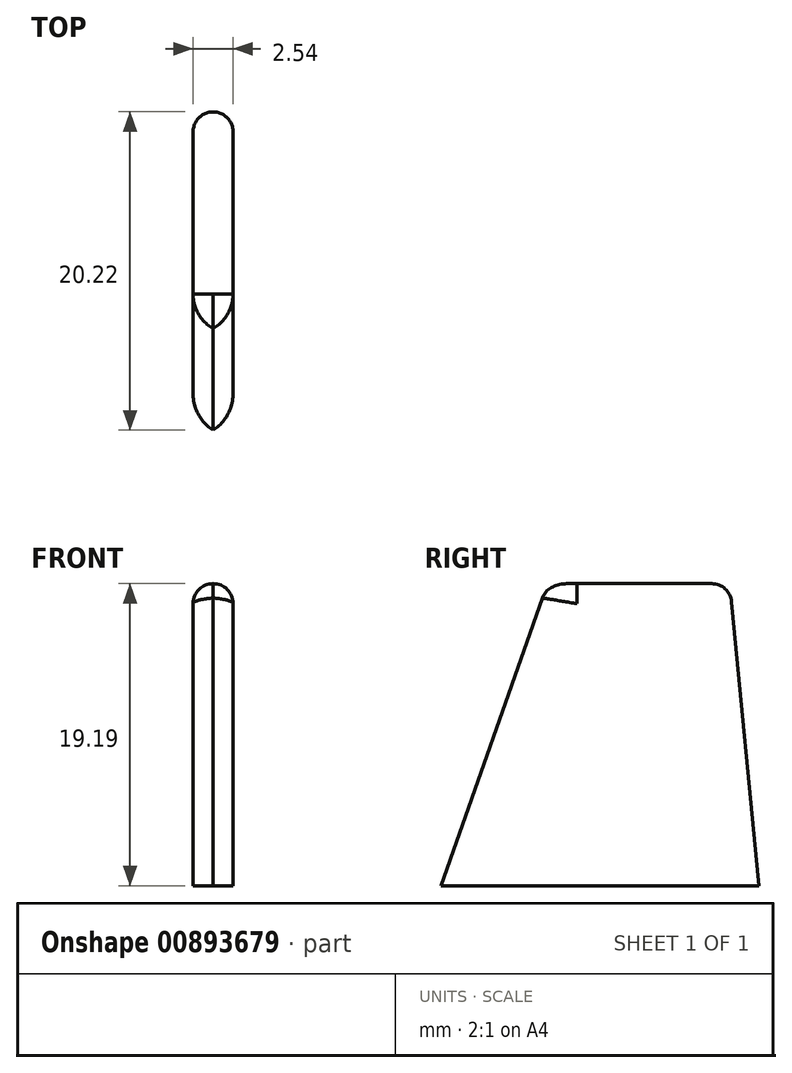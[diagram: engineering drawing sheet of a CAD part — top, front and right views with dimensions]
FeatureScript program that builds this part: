
annotation { "Feature Type Name" : "Feature", "Feature Type Description" : "" }
export const myFeature = defineFeature(function(context is Context, id is Id, definition is map)
    precondition{}
    {
        {
            var Q0;
            Q0=qCreatedBy(makeId("Right.planeOp"),FACE);
            var sketch = newSketch(context, id + "F0", { "sketchPlane" : qUnion([Q0])});
            skLineSegment(sketch, "E0", {"start": v(3.23, 0) * mm, "end": v(23.8, 0) * mm});
            skLineSegment(sketch, "E1", {"start": v(23.8, 0) * mm, "end": v(21.95, 19.19) * mm});
            skLineSegment(sketch, "E2", {"start": v(21.95, 19.19) * mm, "end": v(10, 19.19) * mm});
            skLineSegment(sketch, "E3", {"start": v(10, 19.19) * mm, "end": v(3.23, 0) * mm});
            skSolve(sketch);
        }
        {
            var Q0;
            Q0=makeQuery(id+"F0.imprint","IMPRINT",FACE,{"disambiguationData":[TD([[makeQuery(id+"F0.imprint","IMPRINT",EDGE,{"derivedFrom":sQuery(id+"F0.wireOp",EDGE,"E0")}),1.0]])]});
            extrude(context, id + "F1", {"entities" : qUnion([Q0]), "depth" : 2.54 * mm, "offsetDistance" : 25.4 * mm});
        }
        {
            var Q0;
            Q0=makeQuery(id+"F1.opExtrude","CAP_EDGE",EDGE,{"disambiguationData":[OSD([sQuery(id+"F0.wireOp",EDGE,"E3")])],"isStart":true});
            var Q1;
            Q1=makeQuery(id+"F1.opExtrude","CAP_EDGE",EDGE,{"disambiguationData":[OSD([sQuery(id+"F0.wireOp",EDGE,"E3")])],"isStart":false});
            fillet(context, id + "F2", {"entities" : qUnion([Q0, Q1]), "radius" : 2.54 * mm, "tangentPropagation" : true, "allowEdgeOverflow" : false});
        }
        {
            var Q0;
            Q0=makeQuery(id+"F1.opExtrude","CAP_EDGE",EDGE,{"disambiguationData":[OSD([sQuery(id+"F0.wireOp",EDGE,"E1")])],"isStart":true});
            fillet(context, id + "F3", {"entities" : qUnion([Q0]), "radius" : 1.27 * mm, "tangentPropagation" : true, "allowEdgeOverflow" : false});
        }
        {
            var Q0;
            Q0=makeQuery(id+"F1.opExtrude","CAP_EDGE",EDGE,{"disambiguationData":[OSD([sQuery(id+"F0.wireOp",EDGE,"E1")])],"isStart":false});
            fillet(context, id + "F4", {"entities" : qUnion([Q0]), "radius" : 1.27 * mm, "tangentPropagation" : true, "allowEdgeOverflow" : false});
        }
        {
            var Q0;
            Q0=makeQuery(id+"F1.opExtrude","CAP_EDGE",EDGE,{"disambiguationData":[OSD([sQuery(id+"F0.wireOp",EDGE,"E2")])],"isStart":false});
            var Q1;
            Q1=makeQuery(id+"F1.opExtrude","CAP_EDGE",EDGE,{"disambiguationData":[OSD([sQuery(id+"F0.wireOp",EDGE,"E2")])],"isStart":true});
            fillet(context, id + "F5", {"entities" : qUnion([Q0, Q1]), "radius" : 1.27 * mm, "tangentPropagation" : true, "allowEdgeOverflow" : false});
        }
    });
